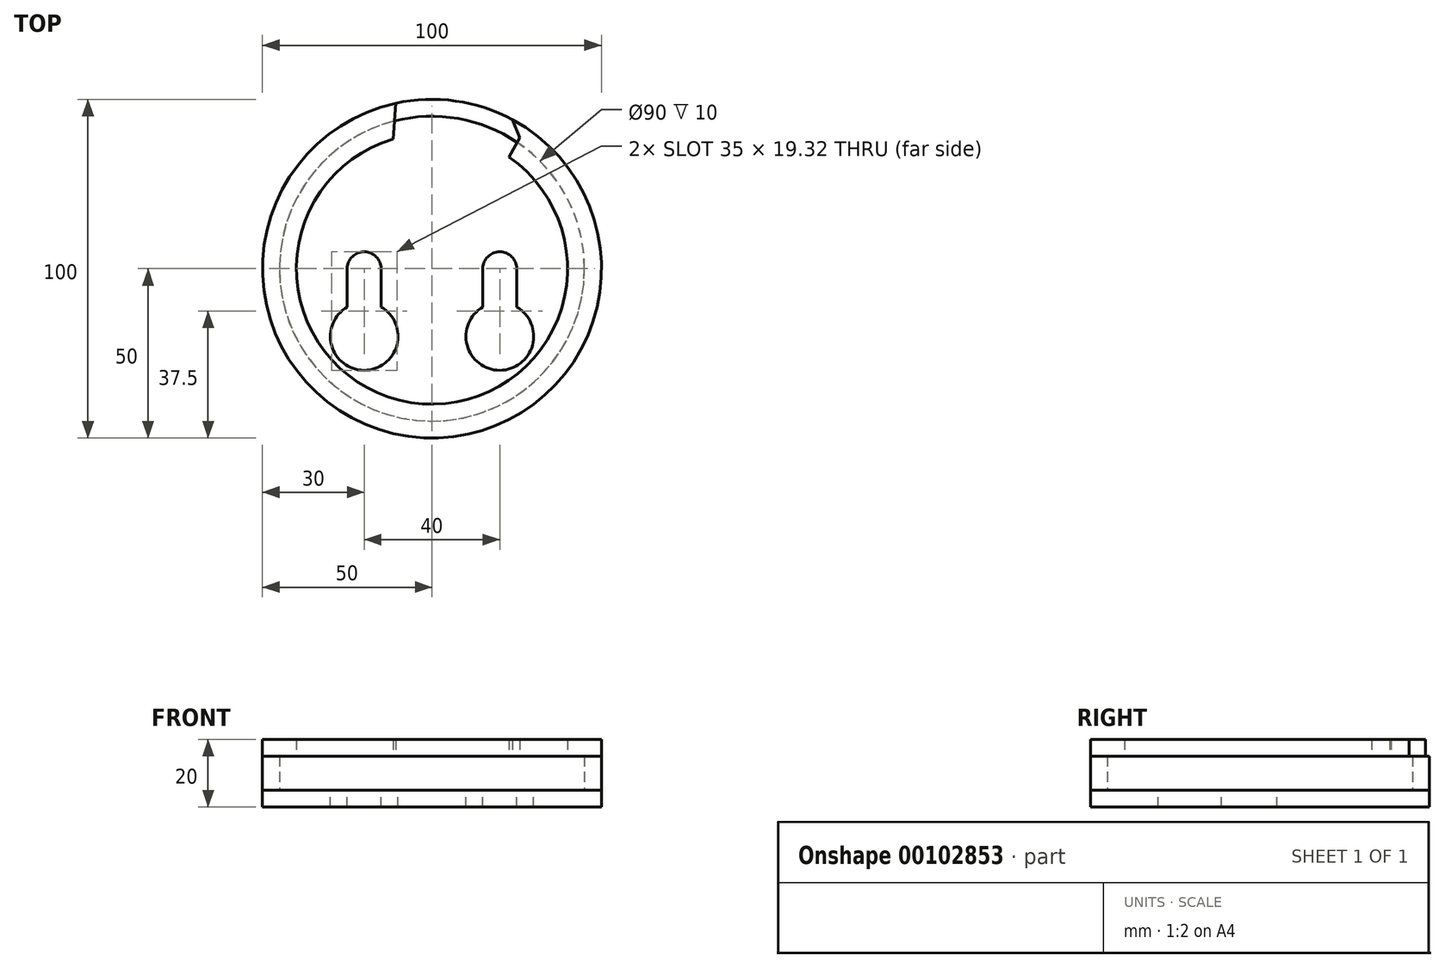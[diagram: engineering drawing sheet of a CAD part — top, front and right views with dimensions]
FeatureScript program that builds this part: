
annotation { "Feature Type Name" : "Feature", "Feature Type Description" : "" }
export const myFeature = defineFeature(function(context is Context, id is Id, definition is map)
    precondition{}
    {
        {
            var Q0;
            Q0=qCreatedBy(makeId("Top.planeOp"),FACE);
            var sketch = newSketch(context, id + "F0", { "sketchPlane" : qUnion([Q0])});
            skCircle(sketch, "E0", {"center": v(0, 0) * mm, "radius": 45 * mm});
            skCircle(sketch, "E1", {"center": v(-20, 0) * mm, "radius": 5 * mm});
            skLineSegment(sketch, "E2", {"start": v(-20, 0) * mm, "end": v(-20, -20) * mm});
            skCircle(sketch, "E3", {"center": v(-20, -20) * mm, "radius": 10 * mm});
            skLineSegment(sketch, "E4", {"start": v(-15, 0) * mm, "end": v(-15, -11.34) * mm});
            skLineSegment(sketch, "E5", {"start": v(-25, 0) * mm, "end": v(-25, -11.34) * mm});
            skLineSegment(sketch, "E6", {"start": v(0, 74.05) * mm, "end": v(0, -67.28) * mm});
            skLineSegment(sketch, "E7.MirrorCS", {"start": v(15, 0) * mm, "end": v(15, -11.34) * mm});
            skCircle(sketch, "E8.MirrorC", {"center": v(20, 0) * mm, "radius": 5 * mm});
            skLineSegment(sketch, "E9.MirrorCS", {"start": v(25, 0) * mm, "end": v(25, -11.34) * mm});
            skCircle(sketch, "E10.MirrorC", {"center": v(20, -20) * mm, "radius": 10 * mm});
            skCircle(sketch, "E11", {"center": v(0, 0) * mm, "radius": 50 * mm});
            skSolve(sketch);
        }
        {
            var Q0;
            {var subQ1=sQuery(id+"F0.wireOp",EDGE,"E7.MirrorCS");Q0=makeQuery(id+"F0.imprint","IMPRINT",FACE,{"disambiguationData":[TD([[makeQuery(id+"F0.imprint","IMPRINT",EDGE,{"derivedFrom":subQ1}),-1.0]])]});}
            var Q1;
            {var subQ0=sQuery(id+"F0.wireOp",EDGE,"E6");var subQ1=sQuery(id+"F0.wireOp",EDGE,"E0");var subQ2=makeQuery(id+"F0.imprint","INTERSECT",VERTEX,{"disambiguationData":[OD(0.0)],"derivedFrom":[subQ1,subQ0]});Q1=makeQuery(id+"F0.imprint","IMPRINT",FACE,{"disambiguationData":[TD([[makeQuery(id+"F0.imprint","IMPRINT",EDGE,{"disambiguationData":[TD([[subQ2,1.0]])],"derivedFrom":subQ1}),-1.0]])]});}
            var Q2;
            {var subQ0=sQuery(id+"F0.wireOp",EDGE,"E6");var subQ1=sQuery(id+"F0.wireOp",EDGE,"E0");var subQ2=makeQuery(id+"F0.imprint","INTERSECT",VERTEX,{"disambiguationData":[OD(0.0)],"derivedFrom":[subQ1,subQ0]});Q2=makeQuery(id+"F0.imprint","IMPRINT",FACE,{"disambiguationData":[TD([[makeQuery(id+"F0.imprint","IMPRINT",EDGE,{"disambiguationData":[TD([[subQ2,-1.0]])],"derivedFrom":subQ1}),-1.0]])]});}
            var Q3;
            {var subQ0=sQuery(id+"F0.wireOp",EDGE,"E4");Q3=makeQuery(id+"F0.imprint","IMPRINT",FACE,{"disambiguationData":[TD([[makeQuery(id+"F0.imprint","IMPRINT",EDGE,{"derivedFrom":subQ0}),1.0]])]});}
            extrude(context, id + "F1", {"entities" : qUnion([Q0, Q1, Q2, Q3]), "oppositeDirection" : true, "depth" : 5 * mm});
        }
        {
            var Q0;
            {var subQ0=sQuery(id+"F0.wireOp",EDGE,"E6");var subQ1=sQuery(id+"F0.wireOp",EDGE,"E0");var subQ2=makeQuery(id+"F0.imprint","INTERSECT",VERTEX,{"disambiguationData":[OD(0.0)],"derivedFrom":[subQ1,subQ0]});Q0=makeQuery(id+"F0.imprint","IMPRINT",FACE,{"disambiguationData":[TD([[makeQuery(id+"F0.imprint","IMPRINT",EDGE,{"disambiguationData":[TD([[subQ2,1.0]])],"derivedFrom":subQ1}),-1.0]])]});}
            var Q1;
            {var subQ0=sQuery(id+"F0.wireOp",EDGE,"E6");var subQ1=sQuery(id+"F0.wireOp",EDGE,"E0");var subQ2=makeQuery(id+"F0.imprint","INTERSECT",VERTEX,{"disambiguationData":[OD(0.0)],"derivedFrom":[subQ1,subQ0]});Q1=makeQuery(id+"F0.imprint","IMPRINT",FACE,{"disambiguationData":[TD([[makeQuery(id+"F0.imprint","IMPRINT",EDGE,{"disambiguationData":[TD([[subQ2,-1.0]])],"derivedFrom":subQ1}),-1.0]])]});}
            extrude(context, id + "F2", {"entities" : qUnion([Q0, Q1]), "depth" : 10 * mm});
        }
        {
            var Q0;
            Q0=makeQuery(id+"F2.opExtrude","CAP_FACE",FACE,{"disambiguationData":[OSD([sQuery(id+"F0.wireOp",EDGE,"E0"),sQuery(id+"F0.wireOp",EDGE,"E11")])],"isStart":false});
            var sketch = newSketch(context, id + "F3", { "sketchPlane" : qUnion([Q0])});
            skCircle(sketch, "E12", {"center": v(0, 0) * mm, "radius": 50 * mm});
            skCircle(sketch, "E13", {"center": v(0, 0) * mm, "radius": 40 * mm});
            skLineSegment(sketch, "E14", {"start": v(-8.32, 39.13) * mm, "end": v(0, 0) * mm, "construction": true});
            skLineSegment(sketch, "E15", {"start": v(0, 40) * mm, "end": v(0, 0) * mm, "construction": true});
            skLineSegment(sketch, "E16", {"start": v(0, 0) * mm, "end": v(-3.6, 39.84) * mm, "construction": true});
            skArc(sketch, "E17.0.startCap", {"start": v(-6.35, 40) * mm, "mid": v(-3, 45.6) * mm, "end": v(3.52, 45.29) * mm});
            skArc(sketch, "E17.0.endCap", {"start": v(6.35, 0) * mm, "mid": v(0, -6.35) * mm, "end": v(-6.35, 0) * mm});
            skLineSegment(sketch, "E17.0.left", {"start": v(6.35, 40) * mm, "end": v(6.35, 38.64) * mm});
            skLineSegment(sketch, "E17.0.right", {"start": v(-6.35, 40) * mm, "end": v(-6.35, 1.41) * mm});
            skCircle(sketch, "E18.cCircle", {"center": v(6.35, 40) * mm, "radius": 17.68 * mm, "construction": true});
            skLineSegment(sketch, "E18.0", {"start": v(19.65, 54.43) * mm, "end": v(25.92, 38.6) * mm});
            skLineSegment(sketch, "E18.1", {"start": v(25.92, 38.6) * mm, "end": v(25.48, 37.82) * mm});
            skLineSegment(sketch, "E18.2", {"start": v(17.46, 23.82) * mm, "end": v(0.63, 21.23) * mm});
            skLineSegment(sketch, "E18.3", {"start": v(0.63, 21.23) * mm, "end": v(-11.9, 32.77) * mm});
            skLineSegment(sketch, "E18.4", {"start": v(-11.9, 32.77) * mm, "end": v(-10.67, 49.75) * mm});
            skLineSegment(sketch, "E18.5", {"start": v(-10.67, 49.75) * mm, "end": v(3.36, 59.4) * mm});
            skLineSegment(sketch, "E18.6", {"start": v(3.36, 59.4) * mm, "end": v(11.5, 56.9) * mm});
            skPoint(sketch, "E18.0.midPoint", {"position": v(22.78, 46.51) * mm});
            skPoint(sketch, "E19.visualSharp", {"position": v(6.35, 0) * mm});
            skLineSegment(sketch, "E19.filletArc", {"start": v(6.35, 0) * mm, "end": v(6.35, 0) * mm});
            skLineSegment(sketch, "E20", {"start": v(-6.35, 1.41) * mm, "end": v(-6.35, 0) * mm});
            skLineSegment(sketch, "E21", {"start": v(25.48, 37.82) * mm, "end": v(17.46, 23.82) * mm});
            skLineSegment(sketch, "E22", {"start": v(6.35, 38.64) * mm, "end": v(6.35, 0) * mm});
            skArc(sketch, "E23", {"start": v(3.52, 45.29) * mm, "mid": v(5.41, 43.32) * mm, "end": v(6.3, 40.74) * mm});
            skLineSegment(sketch, "E24", {"start": v(11.5, 56.9) * mm, "end": v(19.65, 54.43) * mm});
            skArc(sketch, "E25", {"start": v(6.3, 40.74) * mm, "mid": v(6.34, 40.37) * mm, "end": v(6.35, 40) * mm});
            skSolve(sketch);
        }
        {
            var Q0;
            Q0=makeQuery(id+"F3.imprint","IMPRINT",FACE,{"disambiguationData":[TD([[makeQuery(id+"F3.imprint","IMPRINT",EDGE,{"derivedFrom":sQuery(id+"F3.wireOp",EDGE,"E12")}),1.0]])]});
            var Q1;
            Q1=makeQuery(id+"F3.imprint","IMPRINT",FACE,{"disambiguationData":[TD([[makeQuery(id+"F3.imprint","IMPRINT",EDGE,{"derivedFrom":sQuery(id+"F3.wireOp",EDGE,"E13")}),-1.0]])]});
            extrude(context, id + "F4", {"entities" : qUnion([Q0, Q1]), "depth" : 5 * mm});
        }
    });
